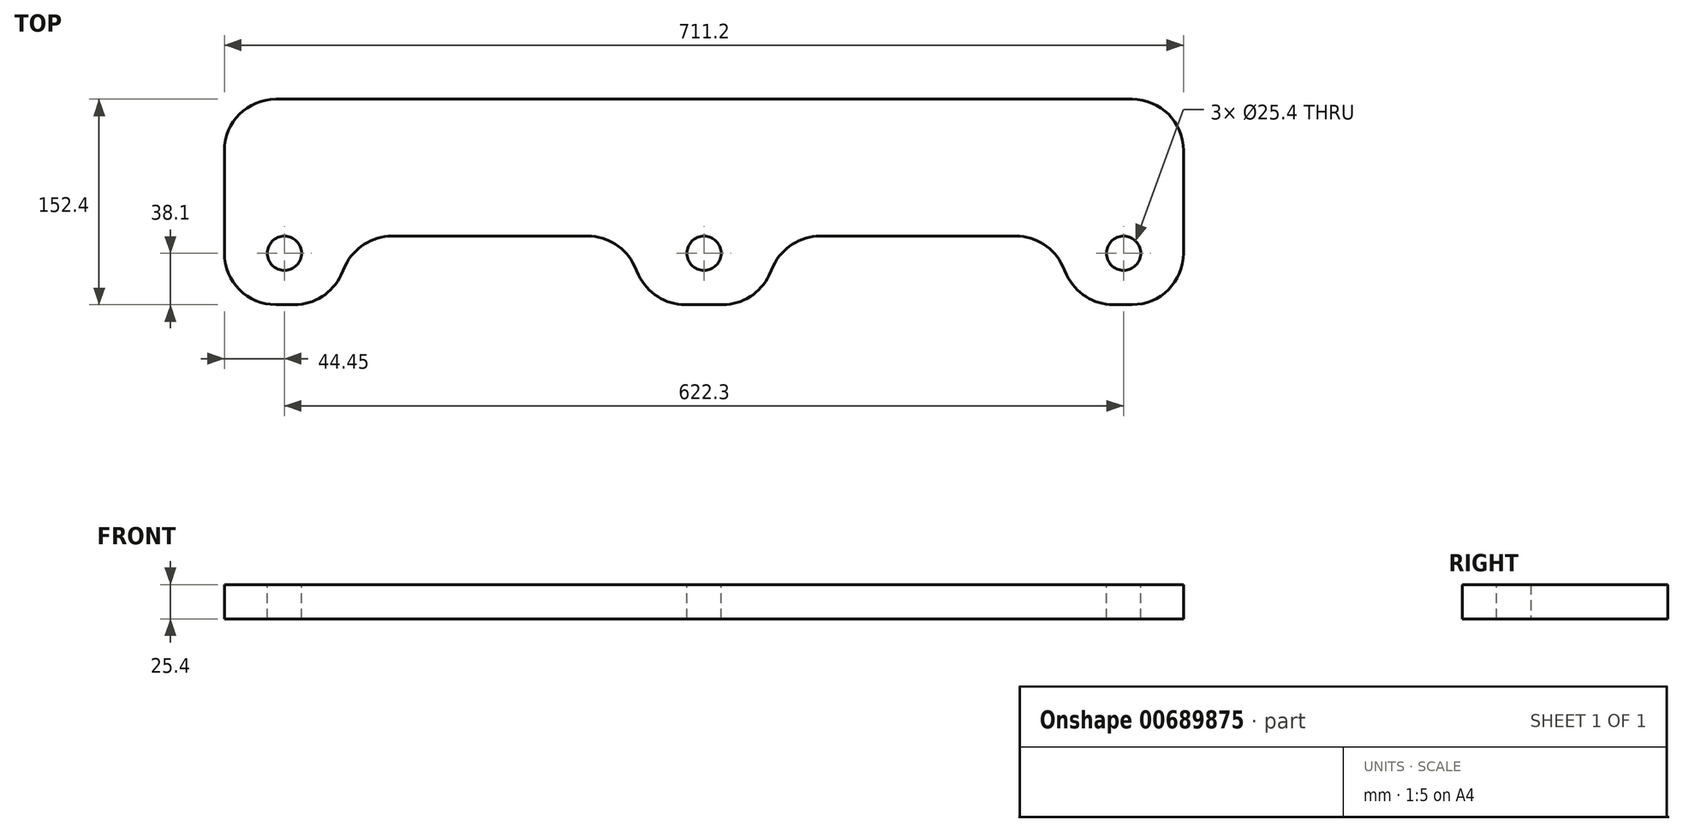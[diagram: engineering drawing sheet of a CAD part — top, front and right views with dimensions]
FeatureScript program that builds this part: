
annotation { "Feature Type Name" : "Feature", "Feature Type Description" : "" }
export const myFeature = defineFeature(function(context is Context, id is Id, definition is map)
    precondition{}
    {
        {
            var Q0;
            Q0=qCreatedBy(makeId("Top.planeOp"),FACE);
            var sketch = newSketch(context, id + "F0", { "sketchPlane" : qUnion([Q0])});
            skLineSegment(sketch, "E0", {"start": v(-355.6, 0) * mm, "end": v(355.6, 0) * mm});
            skLineSegment(sketch, "E1", {"start": v(355.6, 0) * mm, "end": v(355.6, -114.3) * mm});
            skLineSegment(sketch, "E2", {"start": v(317.5, -152.4) * mm, "end": v(303.67, -152.4) * mm});
            skLineSegment(sketch, "E3", {"start": v(269.14, -130.4) * mm, "end": v(265.97, -123.6) * mm});
            skLineSegment(sketch, "E4", {"start": v(231.44, -101.6) * mm, "end": v(86.06, -101.6) * mm});
            skLineSegment(sketch, "E5", {"start": v(51.53, -123.6) * mm, "end": v(48.36, -130.4) * mm});
            skLineSegment(sketch, "E6", {"start": v(13.83, -152.4) * mm, "end": v(-13.83, -152.4) * mm});
            skLineSegment(sketch, "E7", {"start": v(-48.36, -130.4) * mm, "end": v(-51.53, -123.6) * mm});
            skLineSegment(sketch, "E8", {"start": v(-86.06, -101.6) * mm, "end": v(-231.44, -101.6) * mm});
            skLineSegment(sketch, "E9", {"start": v(-265.97, -123.6) * mm, "end": v(-269.14, -130.4) * mm});
            skLineSegment(sketch, "E10", {"start": v(-303.67, -152.4) * mm, "end": v(-317.5, -152.4) * mm});
            skLineSegment(sketch, "E11", {"start": v(-355.6, -114.3) * mm, "end": v(-355.6, 0) * mm});
            skPoint(sketch, "E12.visualSharp", {"position": v(-61.79, -101.6) * mm});
            skArc(sketch, "E12.filletArc", {"start": v(-51.53, -123.6) * mm, "mid": v(-65.59, -107.57) * mm, "end": v(-86.06, -101.6) * mm});
            skPoint(sketch, "E13.visualSharp", {"position": v(61.79, -101.6) * mm});
            skArc(sketch, "E13.filletArc", {"start": v(86.06, -101.6) * mm, "mid": v(65.59, -107.57) * mm, "end": v(51.53, -123.6) * mm});
            skPoint(sketch, "E14.visualSharp", {"position": v(255.71, -101.6) * mm});
            skArc(sketch, "E14.filletArc", {"start": v(265.97, -123.6) * mm, "mid": v(251.91, -107.57) * mm, "end": v(231.44, -101.6) * mm});
            skPoint(sketch, "E15.visualSharp", {"position": v(-255.71, -101.6) * mm});
            skArc(sketch, "E15.filletArc", {"start": v(-231.44, -101.6) * mm, "mid": v(-251.91, -107.57) * mm, "end": v(-265.97, -123.6) * mm});
            skPoint(sketch, "E16.visualSharp", {"position": v(-279.4, -152.4) * mm});
            skArc(sketch, "E16.filletArc", {"start": v(-303.67, -152.4) * mm, "mid": v(-283.2, -146.43) * mm, "end": v(-269.14, -130.4) * mm});
            skPoint(sketch, "E17.visualSharp", {"position": v(-355.6, -152.4) * mm});
            skArc(sketch, "E17.filletArc", {"start": v(-355.6, -114.3) * mm, "mid": v(-344.44, -141.24) * mm, "end": v(-317.5, -152.4) * mm});
            skPoint(sketch, "E18.visualSharp", {"position": v(-38.1, -152.4) * mm});
            skArc(sketch, "E18.filletArc", {"start": v(-48.36, -130.4) * mm, "mid": v(-34.3, -146.43) * mm, "end": v(-13.83, -152.4) * mm});
            skPoint(sketch, "E19.visualSharp", {"position": v(38.1, -152.4) * mm});
            skArc(sketch, "E19.filletArc", {"start": v(13.83, -152.4) * mm, "mid": v(34.3, -146.43) * mm, "end": v(48.36, -130.4) * mm});
            skPoint(sketch, "E20.visualSharp", {"position": v(279.4, -152.4) * mm});
            skArc(sketch, "E20.filletArc", {"start": v(269.14, -130.4) * mm, "mid": v(283.2, -146.43) * mm, "end": v(303.67, -152.4) * mm});
            skPoint(sketch, "E21.visualSharp", {"position": v(355.6, -152.4) * mm});
            skArc(sketch, "E21.filletArc", {"start": v(317.5, -152.4) * mm, "mid": v(344.44, -141.24) * mm, "end": v(355.6, -114.3) * mm});
            skSolve(sketch);
        }
        {
            var Q0;
            Q0=makeQuery(id+"F0.imprint","IMPRINT",FACE,{"disambiguationData":[TD([[makeQuery(id+"F0.imprint","IMPRINT",EDGE,{"derivedFrom":sQuery(id+"F0.wireOp",EDGE,"E0")}),-1.0]])]});
            extrude(context, id + "F1", {"entities" : qUnion([Q0]), "depth" : 25.4 * mm, "offsetDistance" : 25.4 * mm});
        }
        {
            var Q0;
            Q0=makeQuery(id+"F1.opExtrude","SWEPT_EDGE",EDGE,{"disambiguationData":[OSD([sQuery(id+"F0.wireOp",EDGE,"E0"),sQuery(id+"F0.wireOp",EDGE,"E1")])]});
            var Q1;
            Q1=makeQuery(id+"F1.opExtrude","SWEPT_EDGE",EDGE,{"disambiguationData":[OSD([sQuery(id+"F0.wireOp",EDGE,"E0"),sQuery(id+"F0.wireOp",EDGE,"E11")])]});
            fillet(context, id + "F2", {"entities" : qUnion([Q0, Q1]), "radius" : 38.1 * mm, "tangentPropagation" : true, "allowEdgeOverflow" : false});
        }
        {
            var Q0;
            Q0=makeQuery(id+"F1.opExtrude","CAP_FACE",FACE,{"disambiguationData":[OSD([sQuery(id+"F0.wireOp",EDGE,"E0"),sQuery(id+"F0.wireOp",EDGE,"E1"),sQuery(id+"F0.wireOp",EDGE,"E2"),sQuery(id+"F0.wireOp",EDGE,"E3"),sQuery(id+"F0.wireOp",EDGE,"E4"),sQuery(id+"F0.wireOp",EDGE,"E5"),sQuery(id+"F0.wireOp",EDGE,"E6"),sQuery(id+"F0.wireOp",EDGE,"E7"),sQuery(id+"F0.wireOp",EDGE,"E8"),sQuery(id+"F0.wireOp",EDGE,"E9"),sQuery(id+"F0.wireOp",EDGE,"E10"),sQuery(id+"F0.wireOp",EDGE,"E11"),sQuery(id+"F0.wireOp",EDGE,"E12.filletArc"),sQuery(id+"F0.wireOp",EDGE,"E13.filletArc"),sQuery(id+"F0.wireOp",EDGE,"E14.filletArc"),sQuery(id+"F0.wireOp",EDGE,"E15.filletArc"),sQuery(id+"F0.wireOp",EDGE,"E16.filletArc"),sQuery(id+"F0.wireOp",EDGE,"E17.filletArc"),sQuery(id+"F0.wireOp",EDGE,"E18.filletArc"),sQuery(id+"F0.wireOp",EDGE,"E19.filletArc"),sQuery(id+"F0.wireOp",EDGE,"E20.filletArc"),sQuery(id+"F0.wireOp",EDGE,"E21.filletArc")])],"isStart":false});
            var sketch = newSketch(context, id + "F3", { "sketchPlane" : qUnion([Q0])});
            skPoint(sketch, "E22", {"position": v(-311.15, -114.3) * mm});
            skPoint(sketch, "E23", {"position": v(0, -114.3) * mm});
            skPoint(sketch, "E24", {"position": v(311.15, -114.3) * mm});
            skSolve(sketch);
        }
        {
            var Q0;
            Q0=sQuery(id+"F3.wireOp",VERTEX,"E22");
            var Q1;
            Q1=sQuery(id+"F3.wireOp",VERTEX,"E23");
            var Q2;
            Q2=sQuery(id+"F3.wireOp",VERTEX,"E24");
            var Q3;
            Q3=makeQuery(id+"F1.opExtrude","SWEPT_BODY",BODY,{"disambiguationData":[OSD([sQuery(id+"F0.wireOp",EDGE,"E0"),sQuery(id+"F0.wireOp",EDGE,"E1"),sQuery(id+"F0.wireOp",EDGE,"E2"),sQuery(id+"F0.wireOp",EDGE,"E3"),sQuery(id+"F0.wireOp",EDGE,"E4"),sQuery(id+"F0.wireOp",EDGE,"E5"),sQuery(id+"F0.wireOp",EDGE,"E6"),sQuery(id+"F0.wireOp",EDGE,"E7"),sQuery(id+"F0.wireOp",EDGE,"E8"),sQuery(id+"F0.wireOp",EDGE,"E9"),sQuery(id+"F0.wireOp",EDGE,"E10"),sQuery(id+"F0.wireOp",EDGE,"E11"),sQuery(id+"F0.wireOp",EDGE,"E12.filletArc"),sQuery(id+"F0.wireOp",EDGE,"E13.filletArc"),sQuery(id+"F0.wireOp",EDGE,"E14.filletArc"),sQuery(id+"F0.wireOp",EDGE,"E15.filletArc"),sQuery(id+"F0.wireOp",EDGE,"E16.filletArc"),sQuery(id+"F0.wireOp",EDGE,"E17.filletArc"),sQuery(id+"F0.wireOp",EDGE,"E18.filletArc"),sQuery(id+"F0.wireOp",EDGE,"E19.filletArc"),sQuery(id+"F0.wireOp",EDGE,"E20.filletArc"),sQuery(id+"F0.wireOp",EDGE,"E21.filletArc")])]});
            hole(context, id + "F4", {"style" : HoleStyle.SIMPLE, "endStyle" : HoleEndStyle.THROUGH, "standardTappedOrClearance" : lookupTablePath({ "standard" : "ANSI", "size" : "1 (1)", "type" : "Drilled" }), "standardBlindInLast" : lookupTablePath({ "standard" : "ANSI", "size" : "1", "type" : "Drilled" }), "holeDiameter" : 25.4 * mm, "majorDiameter" : 6.35 * mm, "isTappedThrough" : true, "tappedDepth" : 12.7 * mm, "tapClearance" : 3, "locations" : qUnion([Q0, Q1, Q2]), "scope" : qUnion([Q3])});
        }
    });
